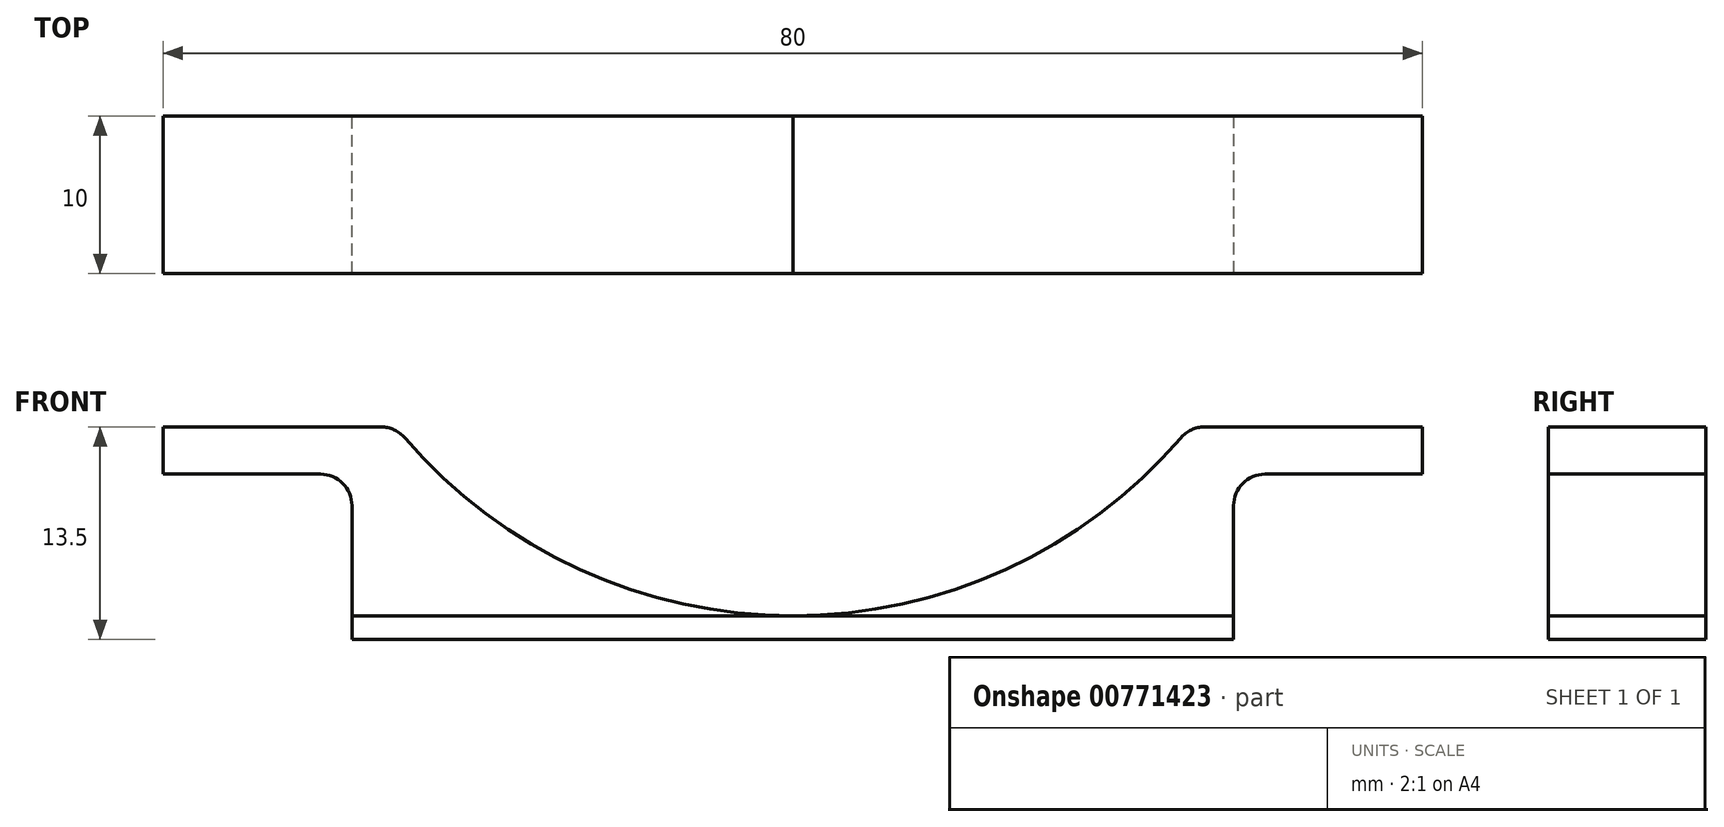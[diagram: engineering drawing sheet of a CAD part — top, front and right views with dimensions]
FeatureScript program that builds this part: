
annotation { "Feature Type Name" : "Feature", "Feature Type Description" : "" }
export const myFeature = defineFeature(function(context is Context, id is Id, definition is map)
    precondition{}
    {
        {
            var Q0;
            Q0=qCreatedBy(makeId("Front.planeOp"),FACE);
            var sketch = newSketch(context, id + "F0", { "sketchPlane" : qUnion([Q0])});
            skArc(sketch, "E0", {"start": v(31.62, 40) * mm, "mid": v(0, 65) * mm, "end": v(-31.62, 40) * mm});
            skLineSegment(sketch, "E1.bottom", {"start": v(-40, 0) * mm, "end": v(40, 0) * mm});
            skLineSegment(sketch, "E1.top", {"start": v(-40, 40) * mm, "end": v(40, 40) * mm});
            skLineSegment(sketch, "E1.left", {"start": v(-40, 0) * mm, "end": v(-40, 40) * mm});
            skLineSegment(sketch, "E1.right", {"start": v(40, 0) * mm, "end": v(40, 40) * mm});
            skLineSegment(sketch, "E2.top", {"start": v(-40, 12) * mm, "end": v(-26.15, 12) * mm});
            skLineSegment(sketch, "E2.left", {"start": v(-40, 0) * mm, "end": v(-40, 12) * mm});
            skLineSegment(sketch, "E2.right", {"start": v(40, 0) * mm, "end": v(40, 12) * mm});
            skLineSegment(sketch, "E3.bottom", {"start": v(-40, 0) * mm, "end": v(-28, 0) * mm});
            skLineSegment(sketch, "E3.top", {"start": v(-40, 9) * mm, "end": v(-30, 9) * mm});
            skLineSegment(sketch, "E3.left", {"start": v(-40, 0) * mm, "end": v(-40, 9) * mm});
            skLineSegment(sketch, "E3.right", {"start": v(-28, 0) * mm, "end": v(-28, 7) * mm});
            skLineSegment(sketch, "E4.bottom", {"start": v(40, 0) * mm, "end": v(28, 0) * mm});
            skLineSegment(sketch, "E4.top", {"start": v(40, 9) * mm, "end": v(30, 9) * mm});
            skLineSegment(sketch, "E4.left", {"start": v(40, 0) * mm, "end": v(40, 9) * mm});
            skLineSegment(sketch, "E4.right", {"start": v(28, 0) * mm, "end": v(28, 7) * mm});
            skPoint(sketch, "E5.visualSharp", {"position": v(-28, 9) * mm});
            skArc(sketch, "E5.filletArc", {"start": v(-28, 7) * mm, "mid": v(-28.59, 8.41) * mm, "end": v(-30, 9) * mm});
            skPoint(sketch, "E6.visualSharp", {"position": v(28, 9) * mm});
            skArc(sketch, "E6.filletArc", {"start": v(30, 9) * mm, "mid": v(28.59, 8.41) * mm, "end": v(28, 7) * mm});
            skArc(sketch, "E7.trimOffspring", {"start": v(-24.64, 11.3) * mm, "mid": v(0, 0) * mm, "end": v(24.64, 11.3) * mm});
            skLineSegment(sketch, "E8.trimOffspring", {"start": v(26.15, 12) * mm, "end": v(40, 12) * mm});
            skPoint(sketch, "E9.visualSharp", {"position": v(-25.22, 12) * mm});
            skArc(sketch, "E9.filletArc", {"start": v(-24.64, 11.3) * mm, "mid": v(-25.32, 11.82) * mm, "end": v(-26.15, 12) * mm});
            skPoint(sketch, "E10.visualSharp", {"position": v(25.22, 12) * mm});
            skArc(sketch, "E10.filletArc", {"start": v(26.15, 12) * mm, "mid": v(25.32, 11.82) * mm, "end": v(24.64, 11.3) * mm});
            skSolve(sketch);
        }
        {
            var Q0;
            {var subQ0=sQuery(id+"F0.wireOp",EDGE,"E2.top");Q0=makeQuery(id+"F0.imprint","IMPRINT",FACE,{"disambiguationData":[TD([[makeQuery(id+"F0.imprint","IMPRINT",EDGE,{"derivedFrom":subQ0}),-1.0]])]});}
            var Q1;
            {var subQ3=sQuery(id+"F0.wireOp",EDGE,"E4.top");Q1=makeQuery(id+"F0.imprint","IMPRINT",FACE,{"disambiguationData":[TD([[makeQuery(id+"F0.imprint","IMPRINT",EDGE,{"derivedFrom":subQ3}),-1.0]])]});}
            extrude(context, id + "F1", {"entities" : qUnion([Q0, Q1]), "depth" : 10 * mm, "offsetDistance" : 25 * mm});
        }
        {
            var Q0;
            Q0=makeQuery(id+"F1.opExtrude","CAP_FACE",FACE,{"disambiguationData":[OSD([sQuery(id+"F0.wireOp",EDGE,"E1.bottom"),sQuery(id+"F0.wireOp",EDGE,"E1.left"),sQuery(id+"F0.wireOp",EDGE,"E2.top"),sQuery(id+"F0.wireOp",EDGE,"E3.top"),sQuery(id+"F0.wireOp",EDGE,"E3.right"),sQuery(id+"F0.wireOp",EDGE,"E5.filletArc"),sQuery(id+"F0.wireOp",EDGE,"E7.trimOffspring"),sQuery(id+"F0.wireOp",EDGE,"E9.filletArc")])],"isStart":false});
            var sketch = newSketch(context, id + "F2", { "sketchPlane" : qUnion([Q0])});
            skLineSegment(sketch, "E11.bottom", {"start": v(-28, 0) * mm, "end": v(28, 0) * mm});
            skLineSegment(sketch, "E11.top", {"start": v(-28, -1.5) * mm, "end": v(28, -1.5) * mm});
            skLineSegment(sketch, "E11.left", {"start": v(-28, 0) * mm, "end": v(-28, -1.5) * mm});
            skLineSegment(sketch, "E11.right", {"start": v(28, 0) * mm, "end": v(28, -1.5) * mm});
            skSolve(sketch);
        }
        {
            var Q0;
            Q0=makeQuery(id+"F2.imprint","IMPRINT",FACE,{"disambiguationData":[TD([[makeQuery(id+"F2.imprint","IMPRINT",EDGE,{"derivedFrom":sQuery(id+"F2.wireOp",EDGE,"E11.top")}),1.0]])]});
            extrude(context, id + "F3", {"entities" : qUnion([Q0]), "oppositeDirection" : true, "depth" : 10 * mm, "offsetDistance" : 25 * mm});
        }
    });
